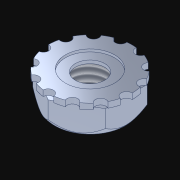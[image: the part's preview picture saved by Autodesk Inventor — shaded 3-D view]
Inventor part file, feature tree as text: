
AUTODESK INVENTOR PART (.ipt)
format: ipt  version: 2021.3 (Build 253353010, 353A)  size: 262,656 bytes
history: native  units: in
note: dims shown in document units (in); Inventor stores cm internally (conversion verified against a paired STEP export)
features: other x2, imported_body x2, thread x1, extrude x1, sketch x1, projected_geometry x1
ambient origin geometry x8: Origin, YZ Plane, XZ Plane, XY Plane, X Axis, Y Axis, Z Axis, Center Point
bodies: Body1 (feature_tree), Body2 (feature_tree)
feature tree (8):
  parser-record x1  (decoder bookkeeping rows leaked as tree rows — omitted from the tree; the rows remain in map.json)
  imported_body  "Base1"
  imported_body  "Base2"
  thread  "Thread1"  [1 undecoded]
  extrude  "Extrusion1"  [1 undecoded]
  other  "NONE_1"
  sketch  "Sketch5"  dims[d6=0.007in d7=0.0in]
  projected_geometry  "Projected Loop1"
note: 2 required parameter values undecoded (feature->parameter linkage not recoverable at this tier; creation-order binding heuristic only, values carry confidence <= 0.55)
